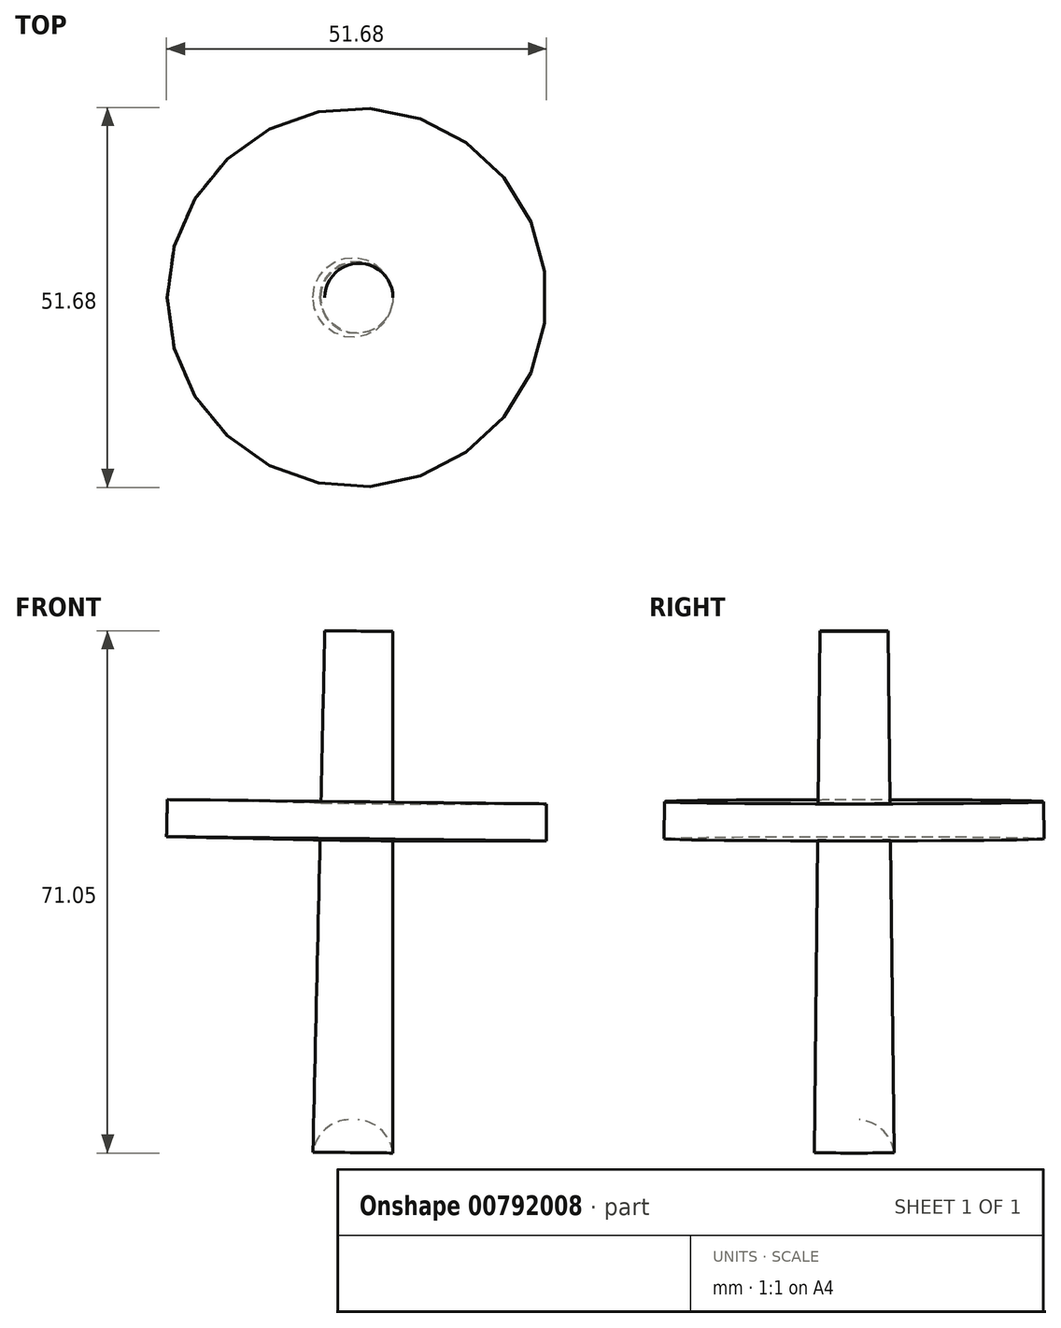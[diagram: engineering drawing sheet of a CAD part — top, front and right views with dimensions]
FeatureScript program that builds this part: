
annotation { "Feature Type Name" : "Feature", "Feature Type Description" : "" }
export const myFeature = defineFeature(function(context is Context, id is Id, definition is map)
    precondition{}
    {
        {
            var Q0;
            Q0=qCreatedBy(makeId("Front.planeOp"),FACE);
            var sketch = newSketch(context, id + "F0", { "sketchPlane" : qUnion([Q0])});
            skArc(sketch, "E0", {"start": v(-5.62, -43.26) * mm, "mid": v(-0.08, -48.2) * mm, "end": v(4.63, -42.47) * mm});
            skLineSegment(sketch, "E1", {"start": v(4.63, -42.47) * mm, "end": v(4.63, 0) * mm});
            skLineSegment(sketch, "E2", {"start": v(4.63, 0) * mm, "end": v(25.52, 0) * mm});
            skLineSegment(sketch, "E3", {"start": v(25.52, 0) * mm, "end": v(25.52, 5.03) * mm});
            skLineSegment(sketch, "E4", {"start": v(25.52, 5.03) * mm, "end": v(4.63, 5.03) * mm});
            skLineSegment(sketch, "E5", {"start": v(4.63, 5.03) * mm, "end": v(4.63, 28.48) * mm});
            skLineSegment(sketch, "E6", {"start": v(4.63, 28.48) * mm, "end": v(0, 28.48) * mm});
            skLineSegment(sketch, "E7", {"start": v(-0.87, -48.2) * mm, "end": v(0, 28.48) * mm});
            skPoint(sketch, "E7.startSnap0", {"position": v(-0.08, -48.2) * mm});
            skSolve(sketch);
        }
        {
            var Q0;
            {var subQ0=sQuery(id+"F0.wireOp",EDGE,"E1");Q0=makeQuery(id+"F0.imprint","IMPRINT",FACE,{"disambiguationData":[TD([[makeQuery(id+"F0.imprint","IMPRINT",EDGE,{"derivedFrom":subQ0}),1.0]])]});}
            var Q1;
            Q1=sQuery(id+"F0.wireOp",EDGE,"E7");
            revolve(context, id + "F1", {"surfaceOperationType" : NewSurfaceOperationType.NEW, "entities" : qUnion([Q0]), "axis" : qUnion([Q1]), "revolveType" : RevolveType.FULL});
        }
    });
